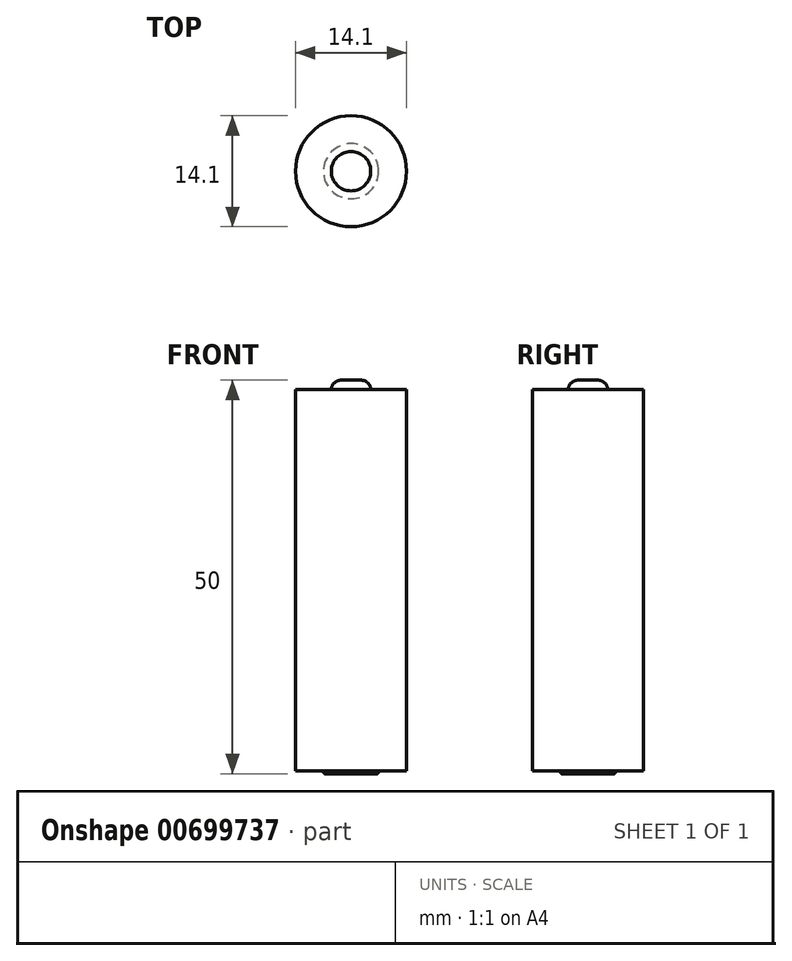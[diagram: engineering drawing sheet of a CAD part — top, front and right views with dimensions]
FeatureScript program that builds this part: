
annotation { "Feature Type Name" : "Feature", "Feature Type Description" : "" }
export const myFeature = defineFeature(function(context is Context, id is Id, definition is map)
    precondition{}
    {
        {
            var Q0;
            Q0=qCreatedBy(makeId("Front.planeOp"),FACE);
            var sketch = newSketch(context, id + "F0", { "sketchPlane" : qUnion([Q0])});
            skLineSegment(sketch, "E0", {"start": v(-20.1, 6.62) * mm, "end": v(-20.1, -41.78) * mm});
            skLineSegment(sketch, "E1", {"start": v(-20.1, -41.78) * mm, "end": v(-13.05, -41.78) * mm});
            skLineSegment(sketch, "E2", {"start": v(-13.05, -41.78) * mm, "end": v(-13.05, 6.62) * mm});
            skLineSegment(sketch, "E3", {"start": v(-14.35, 7.82) * mm, "end": v(-13.05, 7.82) * mm});
            skLineSegment(sketch, "E4", {"start": v(-13.05, 7.82) * mm, "end": v(-13.05, 6.62) * mm});
            skLineSegment(sketch, "E5", {"start": v(-16.55, -41.78) * mm, "end": v(-16.55, -41.93) * mm});
            skLineSegment(sketch, "E6", {"start": v(-16.3, -42.18) * mm, "end": v(-13.05, -42.18) * mm});
            skLineSegment(sketch, "E7", {"start": v(-13.05, -42.18) * mm, "end": v(-13.05, -41.78) * mm});
            skLineSegment(sketch, "E8", {"start": v(-20.1, 6.62) * mm, "end": v(-15.55, 6.62) * mm});
            skLineSegment(sketch, "E9", {"start": v(-15.55, 6.62) * mm, "end": v(-15.55, 6.62) * mm});
            skPoint(sketch, "E10.visualSharp", {"position": v(-15.55, 7.82) * mm});
            skArc(sketch, "E10.filletArc", {"start": v(-14.35, 7.82) * mm, "mid": v(-15.2, 7.47) * mm, "end": v(-15.55, 6.62) * mm});
            skPoint(sketch, "E11.visualSharp", {"position": v(-16.55, -42.18) * mm});
            skArc(sketch, "E11.filletArc", {"start": v(-16.55, -41.93) * mm, "mid": v(-16.47, -42.1) * mm, "end": v(-16.3, -42.18) * mm});
            skSolve(sketch);
        }
        {
            var Q0;
            {var subQ3=sQuery(id+"F0.wireOp",EDGE,"E0");Q0=makeQuery(id+"F0.imprint","IMPRINT",FACE,{"disambiguationData":[TD([[makeQuery(id+"F0.imprint","IMPRINT",EDGE,{"derivedFrom":subQ3}),1.0]])]});}
            var Q1;
            {var subQ1=sQuery(id+"F0.wireOp",EDGE,"E5");Q1=makeQuery(id+"F0.imprint","IMPRINT",FACE,{"disambiguationData":[TD([[makeQuery(id+"F0.imprint","IMPRINT",EDGE,{"derivedFrom":subQ1}),1.0]])]});}
            var Q2;
            Q2=sQuery(id+"F0.wireOp",EDGE,"E2");
            revolve(context, id + "F1", {"entities" : qUnion([Q0, Q1]), "axis" : qUnion([Q2]), "revolveType" : RevolveType.FULL});
        }
    });
